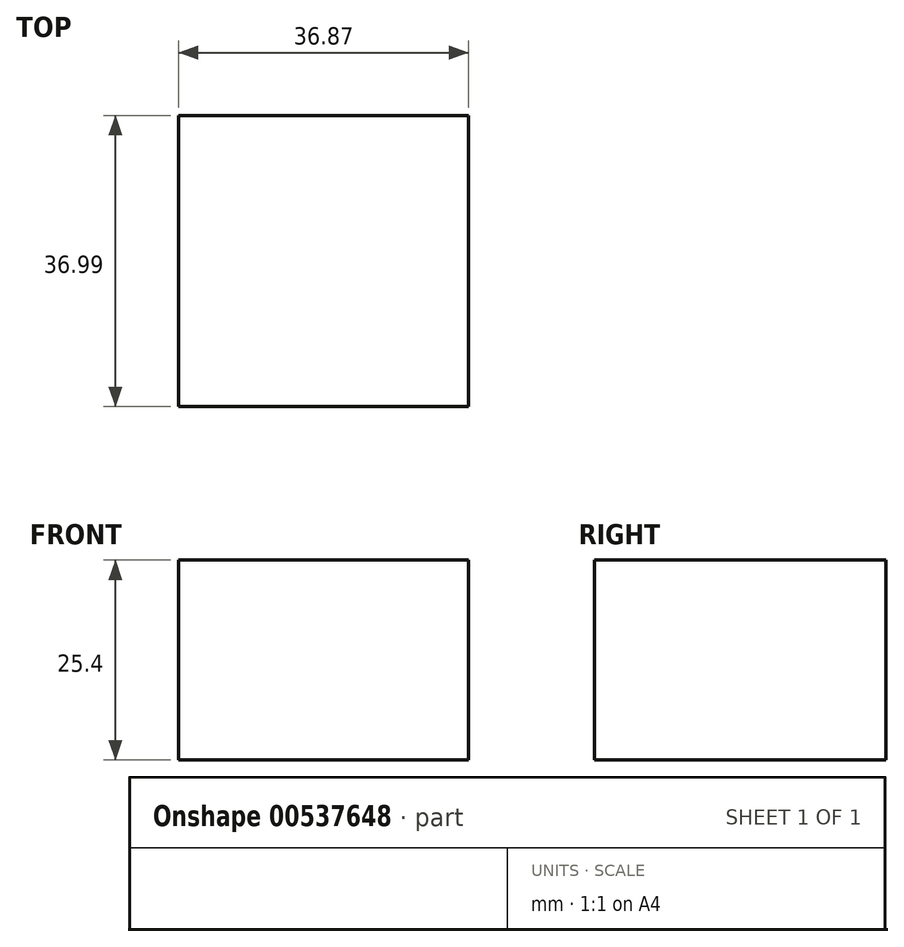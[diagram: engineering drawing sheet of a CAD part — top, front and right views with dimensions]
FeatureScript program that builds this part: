
annotation { "Feature Type Name" : "Feature", "Feature Type Description" : "" }
export const myFeature = defineFeature(function(context is Context, id is Id, definition is map)
    precondition{}
    {
        {
            var Q0;
            Q0=qCreatedBy(makeId("Top.planeOp"),FACE);
            var sketch = newSketch(context, id + "F0", { "sketchPlane" : qUnion([Q0])});
            skLineSegment(sketch, "E0.bottom", {"start": v(0, 0) * mm, "end": v(36.87, 0) * mm});
            skLineSegment(sketch, "E0.top", {"start": v(0, 37) * mm, "end": v(36.87, 37) * mm});
            skLineSegment(sketch, "E0.left", {"start": v(0, 0) * mm, "end": v(0, 37) * mm});
            skLineSegment(sketch, "E0.right", {"start": v(36.87, 0) * mm, "end": v(36.87, 37) * mm});
            skSolve(sketch);
        }
        {
            var Q0;
            Q0=makeQuery(id+"F0.imprint","IMPRINT",FACE,{"disambiguationData":[TD([[makeQuery(id+"F0.imprint","IMPRINT",EDGE,{"derivedFrom":sQuery(id+"F0.wireOp",EDGE,"E0.bottom")}),1.0]])]});
            extrude(context, id + "F1", {"entities" : qUnion([Q0]), "depth" : 25.4 * mm, "offsetDistance" : 25.4 * mm});
        }
    });
